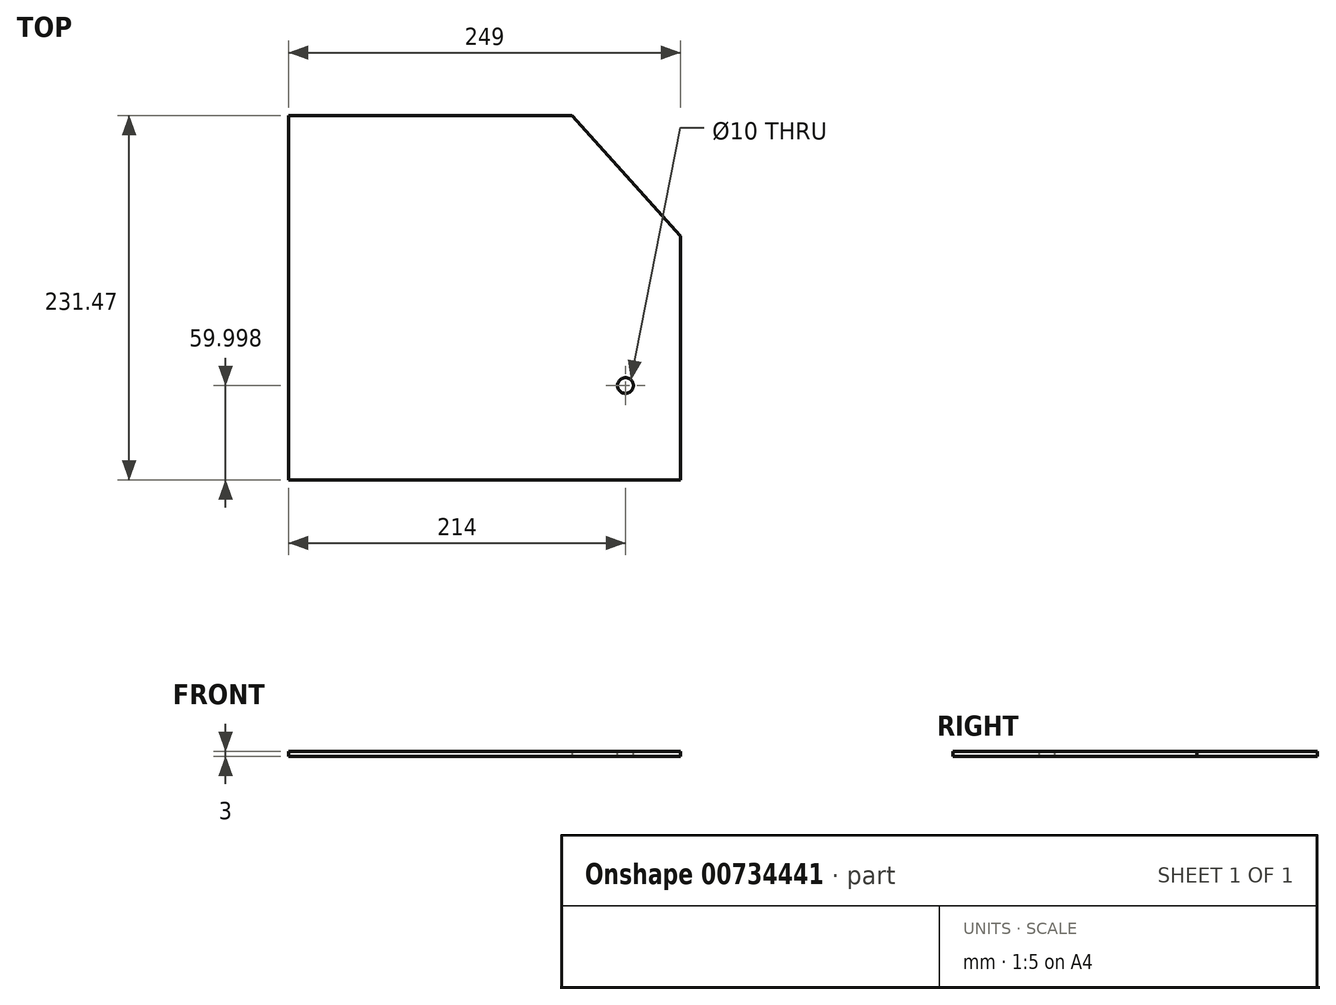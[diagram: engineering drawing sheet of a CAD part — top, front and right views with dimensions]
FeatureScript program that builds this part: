
annotation { "Feature Type Name" : "Feature", "Feature Type Description" : "" }
export const myFeature = defineFeature(function(context is Context, id is Id, definition is map)
    precondition{}
    {
        {
            var Q0;
            Q0=qCreatedBy(makeId("Top.planeOp"),FACE);
            var sketch = newSketch(context, id + "F0", { "sketchPlane" : qUnion([Q0])});
            skLineSegment(sketch, "E0", {"start": v(-249, 98.64) * mm, "end": v(-249, -132.83) * mm});
            skLineSegment(sketch, "E1", {"start": v(-249, -132.83) * mm, "end": v(0, -132.83) * mm});
            skLineSegment(sketch, "E2", {"start": v(0, -132.83) * mm, "end": v(0, 22.17) * mm});
            skLineSegment(sketch, "E3", {"start": v(0, 22.17) * mm, "end": v(-69, 98.64) * mm});
            skLineSegment(sketch, "E4", {"start": v(-249, 98.64) * mm, "end": v(-69, 98.64) * mm});
            skSolve(sketch);
        }
        {
            var Q0;
            Q0=makeQuery(id+"F0.imprint","IMPRINT",FACE,{"disambiguationData":[TD([[makeQuery(id+"F0.imprint","IMPRINT",EDGE,{"derivedFrom":sQuery(id+"F0.wireOp",EDGE,"E0")}),1.0]])]});
            extrude(context, id + "F1", {"entities" : qUnion([Q0]), "depth" : 3 * mm});
        }
        {
            var Q0;
            Q0=makeQuery(id+"F1.opExtrude","CAP_FACE",FACE,{"disambiguationData":[OSD([sQuery(id+"F0.wireOp",EDGE,"E0"),sQuery(id+"F0.wireOp",EDGE,"E1"),sQuery(id+"F0.wireOp",EDGE,"E2"),sQuery(id+"F0.wireOp",EDGE,"E3"),sQuery(id+"F0.wireOp",EDGE,"E4")])],"isStart":false});
            var sketch = newSketch(context, id + "F2", { "sketchPlane" : qUnion([Q0])});
            skCircle(sketch, "E5", {"center": v(-35, -72.83) * mm, "radius": 5 * mm});
            skSolve(sketch);
        }
        {
            var Q0;
            Q0 = qSketchRegion(id + "F2", true);
            extrude(context, id + "F3", {"entities" : qUnion([Q0]), "operationType" : NewBodyOperationType.REMOVE, "oppositeDirection" : true, "depth" : 3 * mm, "offsetDistance" : 25 * mm});
        }
    });
